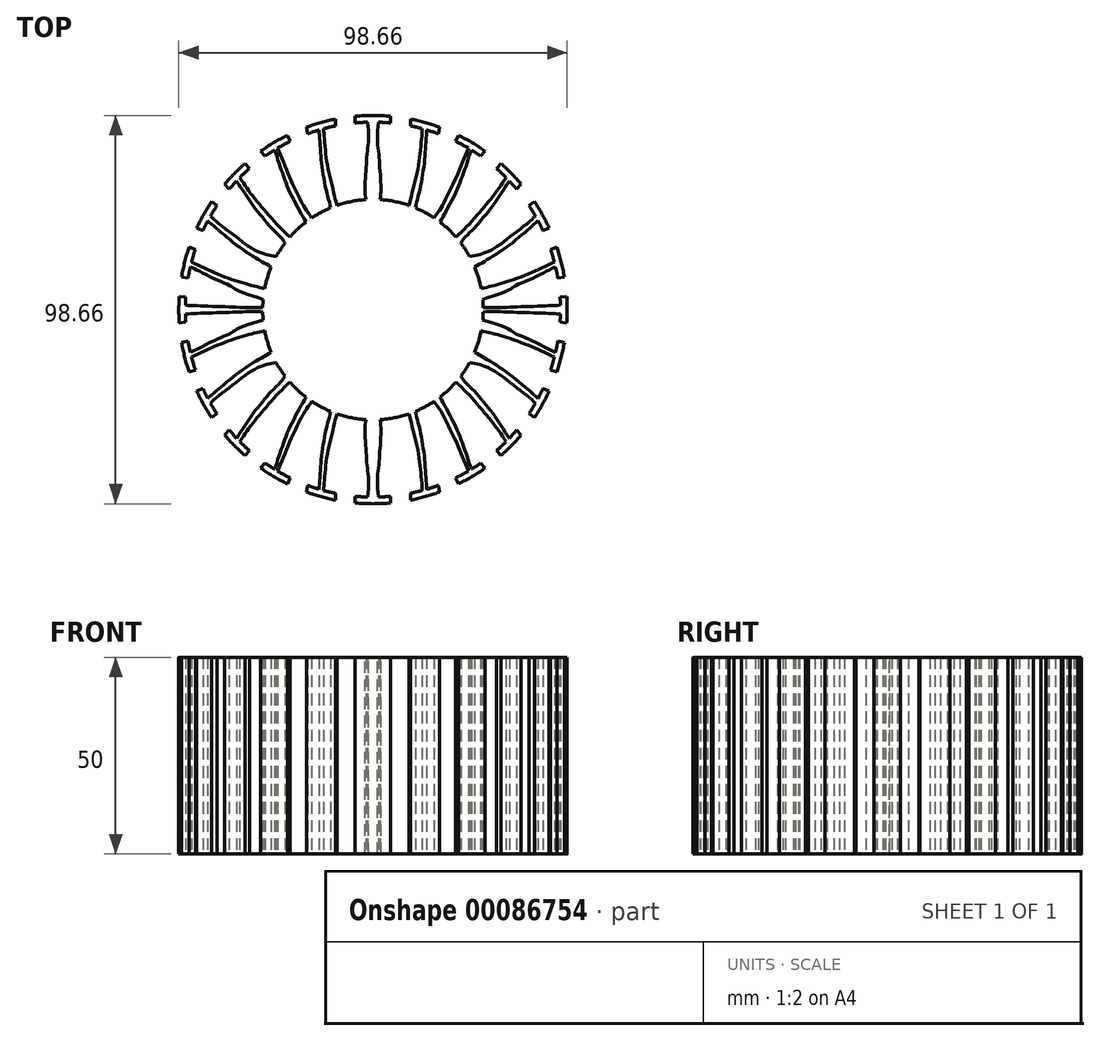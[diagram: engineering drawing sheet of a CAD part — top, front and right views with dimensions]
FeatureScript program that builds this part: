
annotation { "Feature Type Name" : "Feature", "Feature Type Description" : "" }
export const myFeature = defineFeature(function(context is Context, id is Id, definition is map)
    precondition{}
    {
        {
            var Q0;
            Q0=qCreatedBy(makeId("Top.planeOp"),FACE);
            var sketch = newSketch(context, id + "F0", { "sketchPlane" : qUnion([Q0])});
            skArc(sketch, "E0", {"start": v(49.33, 0) * mm, "mid": v(49.3, 1.68) * mm, "end": v(49.21, 3.35) * mm});
            skArc(sketch, "E1", {"start": v(47.63, 1.14) * mm, "mid": v(47.6, 2.16) * mm, "end": v(47.54, 3.17) * mm});
            skLineSegment(sketch, "E2", {"start": v(4.53, 49.12) * mm, "end": v(4.51, 47.43) * mm});
            skLineSegment(sketch, "E3", {"start": v(9.49, 48.4) * mm, "end": v(9.49, 46.69) * mm});
            skLineSegment(sketch, "E4", {"start": v(16.87, 46.35) * mm, "end": v(16.66, 44.64) * mm});
            skLineSegment(sketch, "E5", {"start": v(21.74, 44.28) * mm, "end": v(21, 42.77) * mm});
            skLineSegment(sketch, "E6", {"start": v(28.5, 40.26) * mm, "end": v(27.37, 39) * mm});
            skLineSegment(sketch, "E7", {"start": v(32.51, 37.1) * mm, "end": v(31.39, 35.84) * mm});
            skLineSegment(sketch, "E8", {"start": v(37.66, 31.86) * mm, "end": v(36.52, 30.6) * mm});
            skLineSegment(sketch, "E9", {"start": v(40.98, 27.45) * mm, "end": v(39.63, 26.45) * mm});
            skLineSegment(sketch, "E10", {"start": v(44.76, 20.73) * mm, "end": v(43.2, 20.07) * mm});
            skLineSegment(sketch, "E11", {"start": v(46.7, 15.88) * mm, "end": v(45.12, 15.3) * mm});
            skLineSegment(sketch, "E12", {"start": v(48.62, 8.32) * mm, "end": v(46.97, 8) * mm});
            skLineSegment(sketch, "E13", {"start": v(49.21, 3.35) * mm, "end": v(47.54, 3.17) * mm});
            skArc(sketch, "E14.trimOffspring", {"start": v(4.51, 47.43) * mm, "mid": v(2.94, 47.55) * mm, "end": v(1.37, 47.62) * mm});
            skArc(sketch, "E15.trimOffspring", {"start": v(4.53, 49.12) * mm, "mid": v(2.27, 49.28) * mm, "end": v(0, 49.33) * mm});
            skArc(sketch, "E16.trimOffspring", {"start": v(16.66, 44.64) * mm, "mid": v(15.17, 45.16) * mm, "end": v(13.66, 45.64) * mm});
            skArc(sketch, "E17.trimOffspring", {"start": v(16.87, 46.35) * mm, "mid": v(13.22, 47.52) * mm, "end": v(9.49, 48.4) * mm});
            skArc(sketch, "E18.trimOffspring", {"start": v(28.5, 40.26) * mm, "mid": v(25.2, 42.4) * mm, "end": v(21.74, 44.28) * mm});
            skArc(sketch, "E19.trimOffspring", {"start": v(27.37, 39) * mm, "mid": v(26.22, 39.78) * mm, "end": v(25.04, 40.53) * mm});
            skArc(sketch, "E20.trimOffspring", {"start": v(37.66, 31.86) * mm, "mid": v(35.18, 34.58) * mm, "end": v(32.51, 37.1) * mm});
            skArc(sketch, "E21.trimOffspring", {"start": v(36.52, 30.6) * mm, "mid": v(35.6, 31.66) * mm, "end": v(34.65, 32.7) * mm});
            skArc(sketch, "E22.trimOffspring", {"start": v(44.76, 20.73) * mm, "mid": v(43, 24.16) * mm, "end": v(40.98, 27.45) * mm});
            skArc(sketch, "E23.trimOffspring", {"start": v(43.2, 20.07) * mm, "mid": v(42.6, 21.32) * mm, "end": v(41.96, 22.56) * mm});
            skArc(sketch, "E24.trimOffspring", {"start": v(46.97, 8) * mm, "mid": v(46.7, 9.44) * mm, "end": v(46.39, 10.88) * mm});
            skArc(sketch, "E25.trimOffspring", {"start": v(48.62, 8.32) * mm, "mid": v(47.81, 12.13) * mm, "end": v(46.7, 15.88) * mm});
            skArc(sketch, "E26", {"start": v(9.1, 26.5) * mm, "mid": v(5.5, 27.47) * mm, "end": v(1.8, 27.96) * mm});
            skFitSpline(sketch, "E27", {"points": [v(1.8, 27.96) * mm, v(2, 30.15) * mm, v(1.92, 33.46) * mm, v(1.67, 37.11) * mm, v(1.46, 40.09) * mm, v(1.12, 42.89) * mm, v(1.37, 47.62) * mm], "startDerivative": vector(2.02, 15.22) * mm, "endDerivative": vector(2.38, 25.01) * mm});
            skFitSpline(sketch, "E28", {"points": [v(12.5, 45.97) * mm, v(12.42, 44.08) * mm, v(12.08, 40.51) * mm, v(11.48, 36.1) * mm, v(10.3, 31.08) * mm, v(9.49, 27.64) * mm, v(9.1, 26.5) * mm], "startDerivative": vector(-0.43, -13.47) * mm, "endDerivative": vector(-3.66, -9.72) * mm});
            skFitSpline(sketch, "E29", {"points": [v(10.76, 25.86) * mm, v(11.23, 27.85) * mm, v(11.95, 30.57) * mm, v(12.59, 34.05) * mm, v(13.1, 37.62) * mm, v(13.3, 40.85) * mm, v(13.56, 43.87) * mm, v(13.66, 45.64) * mm], "startDerivative": vector(3.52, 15.97) * mm, "endDerivative": vector(0.48, 14.42) * mm});
            skFitSpline(sketch, "E30", {"points": [v(24.26, 41) * mm, v(22.57, 36.98) * mm, v(20.7, 32.6) * mm, v(19.17, 29.47) * mm, v(17.56, 26.28) * mm, v(16.28, 24.41) * mm, v(15.54, 23.31) * mm], "startDerivative": vector(-8.46, -20.08) * mm, "endDerivative": vector(-6.5, -9.86) * mm});
            skFitSpline(sketch, "E31", {"points": [v(17, 22.26) * mm, v(18.28, 24.45) * mm, v(20.15, 27.98) * mm, v(21.76, 31.38) * mm, v(22.87, 34.35) * mm, v(23.89, 37.15) * mm, v(24.7, 39.79) * mm, v(25.04, 40.53) * mm], "startDerivative": vector(8.93, 14.97) * mm, "endDerivative": vector(4.14, 7.56) * mm});
            skFitSpline(sketch, "E32", {"points": [v(21.1, 18.43) * mm, v(24.01, 21.27) * mm, v(26.99, 24.58) * mm, v(29.37, 27.43) * mm, v(31.53, 30.15) * mm, v(33.02, 32.31) * mm, v(33.83, 33.55) * mm], "startDerivative": vector(15.59, 14.62) * mm, "endDerivative": vector(6.66, 10.2) * mm});
            skFitSpline(sketch, "E33", {"points": [v(34.65, 32.7) * mm, v(32.33, 29.17) * mm, v(30.23, 26.13) * mm, v(27.73, 23.02) * mm, v(25.4, 20.35) * mm, v(23.37, 18.37) * mm, v(22.34, 16.9) * mm], "startDerivative": vector(-12.39, -19.06) * mm, "endDerivative": vector(-7.33, -11.9) * mm});
            skFitSpline(sketch, "E34", {"points": [v(24.55, 13.49) * mm, v(26.54, 13.83) * mm, v(28.7, 14.51) * mm, v(32.04, 16.38) * mm, v(35.67, 19.22) * mm, v(39.64, 22.22) * mm, v(41.26, 23.83) * mm], "startDerivative": vector(15.26, 2.35) * mm, "endDerivative": vector(9.78, 10.81) * mm});
            skFitSpline(sketch, "E35", {"points": [v(41.96, 22.56) * mm, v(39.36, 20.3) * mm, v(34.3, 16.15) * mm, v(28.98, 12.64) * mm, v(25.83, 10.85) * mm], "startDerivative": vector(-11.26, -9.89) * mm, "endDerivative": vector(-13.8, -7.6) * mm});
            skFitSpline(sketch, "E36", {"points": [v(27.5, 5.38) * mm, v(31.98, 6.46) * mm, v(39.24, 8.95) * mm, v(46.08, 12.1) * mm], "startDerivative": vector(15.05, 3.25) * mm, "endDerivative": vector(18.54, 9.06) * mm});
            skFitSpline(sketch, "E37", {"points": [v(46.39, 10.88) * mm, v(44.54, 9.96) * mm, v(39.57, 7.5) * mm, v(36.08, 6) * mm, v(34.72, 5.06) * mm, v(27.9, 2.6) * mm], "startDerivative": vector(-10.67, -5.18) * mm, "endDerivative": vector(-30.07, -9.49) * mm});
            skFitSpline(sketch, "E38", {"points": [v(47.63, 1.14) * mm, v(43.46, 0.92) * mm, v(36.2, 0.67) * mm, v(31.63, 0.53) * mm, v(28, 0.56) * mm], "startDerivative": vector(-16.21, -0.96) * mm, "endDerivative": vector(-16.65, 0.32) * mm});
            skArc(sketch, "E39.trimOffspring", {"start": v(46.08, 12.1) * mm, "mid": v(45.63, 13.7) * mm, "end": v(45.12, 15.3) * mm});
            skArc(sketch, "E40.trimOffspring", {"start": v(41.26, 23.83) * mm, "mid": v(40.46, 25.15) * mm, "end": v(39.63, 26.45) * mm});
            skArc(sketch, "E41.trimOffspring", {"start": v(33.83, 33.55) * mm, "mid": v(32.63, 34.72) * mm, "end": v(31.39, 35.84) * mm});
            skArc(sketch, "E42.trimOffspring", {"start": v(24.26, 41) * mm, "mid": v(22.64, 41.92) * mm, "end": v(21, 42.77) * mm});
            skArc(sketch, "E43.trimOffspring", {"start": v(12.5, 45.97) * mm, "mid": v(11, 46.35) * mm, "end": v(9.49, 46.69) * mm});
            skArc(sketch, "E44.trimOffspring", {"start": v(15.54, 23.31) * mm, "mid": v(13.21, 24.7) * mm, "end": v(10.76, 25.86) * mm});
            skArc(sketch, "E45.trimOffspring", {"start": v(21.1, 18.43) * mm, "mid": v(19.15, 20.45) * mm, "end": v(17, 22.26) * mm});
            skArc(sketch, "E46.trimOffspring", {"start": v(24.55, 13.49) * mm, "mid": v(23.5, 15.23) * mm, "end": v(22.34, 16.9) * mm});
            skArc(sketch, "E47.trimOffspring", {"start": v(27.5, 5.38) * mm, "mid": v(26.8, 8.16) * mm, "end": v(25.83, 10.85) * mm});
            skArc(sketch, "E48.trimOffspring", {"start": v(28, 0.56) * mm, "mid": v(27.97, 1.58) * mm, "end": v(27.9, 2.6) * mm});
            skLineSegment(sketch, "E49", {"start": v(0, 49.33) * mm, "end": v(0, 0) * mm});
            skLineSegment(sketch, "E50", {"start": v(49.33, 0) * mm, "end": v(0, 0) * mm});
            skArc(sketch, "E51.MirrorCS", {"start": v(-28, 0.56) * mm, "mid": v(-27.97, 1.58) * mm, "end": v(-27.9, 2.6) * mm});
            skArc(sketch, "E52.MirrorCS", {"start": v(-27.37, 39) * mm, "mid": v(-26.22, 39.78) * mm, "end": v(-25.04, 40.53) * mm});
            skArc(sketch, "E53.MirrorCS", {"start": v(-12.5, 45.97) * mm, "mid": v(-11, 46.35) * mm, "end": v(-9.49, 46.69) * mm});
            skArc(sketch, "E54.MirrorCS", {"start": v(-16.66, 44.64) * mm, "mid": v(-15.17, 45.16) * mm, "end": v(-13.66, 45.64) * mm});
            skArc(sketch, "E55.MirrorCS", {"start": v(-41.26, 23.83) * mm, "mid": v(-40.46, 25.15) * mm, "end": v(-39.63, 26.45) * mm});
            skArc(sketch, "E56.MirrorCS", {"start": v(-16.87, 46.35) * mm, "mid": v(-13.22, 47.52) * mm, "end": v(-9.49, 48.4) * mm});
            skArc(sketch, "E57.MirrorCS", {"start": v(-21.1, 18.43) * mm, "mid": v(-19.15, 20.45) * mm, "end": v(-17, 22.26) * mm});
            skArc(sketch, "E58.MirrorCS", {"start": v(-15.54, 23.31) * mm, "mid": v(-13.21, 24.7) * mm, "end": v(-10.76, 25.86) * mm});
            skArc(sketch, "E59.MirrorCS", {"start": v(-36.52, 30.6) * mm, "mid": v(-35.6, 31.66) * mm, "end": v(-34.65, 32.7) * mm});
            skArc(sketch, "E60.MirrorCS", {"start": v(-24.55, 13.49) * mm, "mid": v(-23.5, 15.23) * mm, "end": v(-22.34, 16.9) * mm});
            skArc(sketch, "E61.MirrorCS", {"start": v(-27.5, 5.38) * mm, "mid": v(-26.8, 8.16) * mm, "end": v(-25.83, 10.85) * mm});
            skLineSegment(sketch, "E62.MirrorCS", {"start": v(-49.21, 3.35) * mm, "end": v(-47.54, 3.17) * mm});
            skArc(sketch, "E63.MirrorCS", {"start": v(-4.51, 47.43) * mm, "mid": v(-2.94, 47.55) * mm, "end": v(-1.37, 47.62) * mm});
            skArc(sketch, "E64.MirrorCS", {"start": v(-4.53, 49.12) * mm, "mid": v(-2.27, 49.28) * mm, "end": v(0, 49.33) * mm});
            skArc(sketch, "E65.MirrorCS", {"start": v(-49.33, 0) * mm, "mid": v(-49.3, 1.68) * mm, "end": v(-49.21, 3.35) * mm});
            skArc(sketch, "E66.MirrorCS", {"start": v(-47.63, 1.14) * mm, "mid": v(-47.6, 2.16) * mm, "end": v(-47.54, 3.17) * mm});
            skLineSegment(sketch, "E67.MirrorCS", {"start": v(-16.87, 46.35) * mm, "end": v(-16.66, 44.64) * mm});
            skLineSegment(sketch, "E68.MirrorCS", {"start": v(-44.76, 20.73) * mm, "end": v(-43.2, 20.07) * mm});
            skArc(sketch, "E69.MirrorCS", {"start": v(-43.2, 20.07) * mm, "mid": v(-42.6, 21.32) * mm, "end": v(-41.96, 22.56) * mm});
            skArc(sketch, "E70.MirrorCS", {"start": v(-33.83, 33.55) * mm, "mid": v(-32.63, 34.72) * mm, "end": v(-31.39, 35.84) * mm});
            skArc(sketch, "E71.MirrorCS", {"start": v(-24.26, 41) * mm, "mid": v(-22.64, 41.92) * mm, "end": v(-21, 42.77) * mm});
            skArc(sketch, "E72.MirrorCS", {"start": v(-37.66, 31.86) * mm, "mid": v(-35.18, 34.58) * mm, "end": v(-32.51, 37.1) * mm});
            skArc(sketch, "E73.MirrorCS", {"start": v(-44.76, 20.73) * mm, "mid": v(-43, 24.16) * mm, "end": v(-40.98, 27.45) * mm});
            skLineSegment(sketch, "E74.MirrorCS", {"start": v(-4.53, 49.12) * mm, "end": v(-4.51, 47.43) * mm});
            skLineSegment(sketch, "E75.MirrorCS", {"start": v(-9.49, 48.4) * mm, "end": v(-9.49, 46.69) * mm});
            skLineSegment(sketch, "E76.MirrorCS", {"start": v(-21.74, 44.28) * mm, "end": v(-21, 42.77) * mm});
            skLineSegment(sketch, "E77.MirrorCS", {"start": v(-28.5, 40.26) * mm, "end": v(-27.37, 39) * mm});
            skLineSegment(sketch, "E78.MirrorCS", {"start": v(-32.51, 37.1) * mm, "end": v(-31.39, 35.84) * mm});
            skLineSegment(sketch, "E79.MirrorCS", {"start": v(-37.66, 31.86) * mm, "end": v(-36.52, 30.6) * mm});
            skLineSegment(sketch, "E80.MirrorCS", {"start": v(-40.98, 27.45) * mm, "end": v(-39.63, 26.45) * mm});
            skLineSegment(sketch, "E81.MirrorCS", {"start": v(-46.7, 15.88) * mm, "end": v(-45.12, 15.3) * mm});
            skLineSegment(sketch, "E82.MirrorCS", {"start": v(-48.62, 8.32) * mm, "end": v(-46.97, 8) * mm});
            skArc(sketch, "E83.MirrorCS", {"start": v(-46.08, 12.1) * mm, "mid": v(-45.63, 13.7) * mm, "end": v(-45.12, 15.3) * mm});
            skArc(sketch, "E84.MirrorCS", {"start": v(-46.97, 8) * mm, "mid": v(-46.7, 9.44) * mm, "end": v(-46.39, 10.88) * mm});
            skArc(sketch, "E85.MirrorCS", {"start": v(-48.62, 8.32) * mm, "mid": v(-47.81, 12.13) * mm, "end": v(-46.7, 15.88) * mm});
            skArc(sketch, "E86.MirrorCS", {"start": v(-28.5, 40.26) * mm, "mid": v(-25.2, 42.4) * mm, "end": v(-21.74, 44.28) * mm});
            skArc(sketch, "E87.MirrorCS", {"start": v(-9.1, 26.5) * mm, "mid": v(-5.5, 27.47) * mm, "end": v(-1.8, 27.96) * mm});
            skFitSpline(sketch, "E88.MirrorCS", {"points": [v(-41.96, 22.56) * mm, v(-39.36, 20.3) * mm, v(-34.3, 16.15) * mm, v(-28.98, 12.64) * mm, v(-25.83, 10.85) * mm], "startDerivative": vector(11.26, -9.89) * mm, "endDerivative": vector(13.8, -7.6) * mm});
            skFitSpline(sketch, "E89.MirrorCS", {"points": [v(-1.8, 27.96) * mm, v(-2, 30.15) * mm, v(-1.92, 33.46) * mm, v(-1.67, 37.11) * mm, v(-1.46, 40.09) * mm, v(-1.12, 42.89) * mm, v(-1.37, 47.62) * mm], "startDerivative": vector(-2.02, 15.22) * mm, "endDerivative": vector(-2.38, 25.01) * mm});
            skFitSpline(sketch, "E90.MirrorCS", {"points": [v(-10.76, 25.86) * mm, v(-11.23, 27.85) * mm, v(-11.95, 30.57) * mm, v(-12.59, 34.05) * mm, v(-13.1, 37.62) * mm, v(-13.3, 40.85) * mm, v(-13.56, 43.87) * mm, v(-13.66, 45.64) * mm], "startDerivative": vector(-3.52, 15.97) * mm, "endDerivative": vector(-0.48, 14.42) * mm});
            skFitSpline(sketch, "E91.MirrorCS", {"points": [v(-27.5, 5.38) * mm, v(-31.98, 6.46) * mm, v(-39.24, 8.95) * mm, v(-46.08, 12.1) * mm], "startDerivative": vector(-15.05, 3.25) * mm, "endDerivative": vector(-18.54, 9.06) * mm});
            skFitSpline(sketch, "E92.MirrorCS", {"points": [v(-12.5, 45.97) * mm, v(-12.42, 44.08) * mm, v(-12.08, 40.51) * mm, v(-11.48, 36.1) * mm, v(-10.3, 31.08) * mm, v(-9.49, 27.64) * mm, v(-9.1, 26.5) * mm], "startDerivative": vector(0.43, -13.47) * mm, "endDerivative": vector(3.66, -9.72) * mm});
            skFitSpline(sketch, "E93.MirrorCS", {"points": [v(-24.26, 41) * mm, v(-22.57, 36.98) * mm, v(-20.7, 32.6) * mm, v(-19.17, 29.47) * mm, v(-17.56, 26.28) * mm, v(-16.28, 24.41) * mm, v(-15.54, 23.31) * mm], "startDerivative": vector(8.46, -20.08) * mm, "endDerivative": vector(6.5, -9.86) * mm});
            skFitSpline(sketch, "E94.MirrorCS", {"points": [v(-46.39, 10.88) * mm, v(-44.54, 9.96) * mm, v(-39.57, 7.5) * mm, v(-36.08, 6) * mm, v(-34.72, 5.06) * mm, v(-27.9, 2.6) * mm], "startDerivative": vector(10.67, -5.18) * mm, "endDerivative": vector(30.07, -9.49) * mm});
            skFitSpline(sketch, "E95.MirrorCS", {"points": [v(-17, 22.26) * mm, v(-18.28, 24.45) * mm, v(-20.15, 27.98) * mm, v(-21.76, 31.38) * mm, v(-22.87, 34.35) * mm, v(-23.89, 37.15) * mm, v(-24.7, 39.79) * mm, v(-25.04, 40.53) * mm], "startDerivative": vector(-8.93, 14.97) * mm, "endDerivative": vector(-4.14, 7.56) * mm});
            skFitSpline(sketch, "E96.MirrorCS", {"points": [v(-21.1, 18.43) * mm, v(-24.01, 21.27) * mm, v(-26.99, 24.58) * mm, v(-29.37, 27.43) * mm, v(-31.53, 30.15) * mm, v(-33.02, 32.31) * mm, v(-33.83, 33.55) * mm], "startDerivative": vector(-15.59, 14.62) * mm, "endDerivative": vector(-6.66, 10.2) * mm});
            skFitSpline(sketch, "E97.MirrorCS", {"points": [v(-34.65, 32.7) * mm, v(-32.33, 29.17) * mm, v(-30.23, 26.13) * mm, v(-27.73, 23.02) * mm, v(-25.4, 20.35) * mm, v(-23.37, 18.37) * mm, v(-22.34, 16.9) * mm], "startDerivative": vector(12.39, -19.06) * mm, "endDerivative": vector(7.33, -11.9) * mm});
            skFitSpline(sketch, "E98.MirrorCS", {"points": [v(-24.55, 13.49) * mm, v(-26.54, 13.83) * mm, v(-28.7, 14.51) * mm, v(-32.04, 16.38) * mm, v(-35.67, 19.22) * mm, v(-39.64, 22.22) * mm, v(-41.26, 23.83) * mm], "startDerivative": vector(-15.26, 2.35) * mm, "endDerivative": vector(-9.78, 10.81) * mm});
            skFitSpline(sketch, "E99.MirrorCS", {"points": [v(-47.63, 1.14) * mm, v(-43.46, 0.92) * mm, v(-36.2, 0.67) * mm, v(-31.63, 0.53) * mm, v(-28, 0.56) * mm], "startDerivative": vector(16.21, -0.96) * mm, "endDerivative": vector(16.65, 0.32) * mm});
            skLineSegment(sketch, "E100.MirrorCS", {"start": v(-49.33, 0) * mm, "end": v(0, 0) * mm});
            skLineSegment(sketch, "E101", {"start": v(0, 0) * mm, "end": v(-91, 0) * mm, "construction": true});
            skArc(sketch, "E102.MirrorCS", {"start": v(-47.63, -1.14) * mm, "mid": v(-47.6, -2.16) * mm, "end": v(-47.54, -3.17) * mm});
            skArc(sketch, "E103.MirrorCS", {"start": v(-33.83, -33.55) * mm, "mid": v(-32.63, -34.72) * mm, "end": v(-31.39, -35.84) * mm});
            skLineSegment(sketch, "E104.MirrorCS", {"start": v(-44.76, -20.73) * mm, "end": v(-43.2, -20.07) * mm});
            skArc(sketch, "E105.MirrorCS", {"start": v(-28, -0.56) * mm, "mid": v(-27.97, -1.58) * mm, "end": v(-27.9, -2.6) * mm});
            skArc(sketch, "E106.MirrorCS", {"start": v(27.37, -39) * mm, "mid": v(26.22, -39.78) * mm, "end": v(25.04, -40.53) * mm});
            skArc(sketch, "E107.MirrorCS", {"start": v(-36.52, -30.6) * mm, "mid": v(-35.6, -31.66) * mm, "end": v(-34.65, -32.7) * mm});
            skLineSegment(sketch, "E108.MirrorCS", {"start": v(-49.21, -3.35) * mm, "end": v(-47.54, -3.17) * mm});
            skLineSegment(sketch, "E109.MirrorCS", {"start": v(-37.66, -31.86) * mm, "end": v(-36.52, -30.6) * mm});
            skLineSegment(sketch, "E110.MirrorCS", {"start": v(49.21, -3.35) * mm, "end": v(47.54, -3.17) * mm});
            skArc(sketch, "E111.MirrorCS", {"start": v(49.33, 0) * mm, "mid": v(49.3, -1.68) * mm, "end": v(49.21, -3.35) * mm});
            skArc(sketch, "E112.MirrorCS", {"start": v(47.63, -1.14) * mm, "mid": v(47.6, -2.16) * mm, "end": v(47.54, -3.17) * mm});
            skArc(sketch, "E113.MirrorCS", {"start": v(28, -0.56) * mm, "mid": v(27.97, -1.58) * mm, "end": v(27.9, -2.6) * mm});
            skArc(sketch, "E114.MirrorCS", {"start": v(-49.33, 0) * mm, "mid": v(-49.3, -1.68) * mm, "end": v(-49.21, -3.35) * mm});
            skArc(sketch, "E115.MirrorCS", {"start": v(-24.26, -41) * mm, "mid": v(-22.64, -41.92) * mm, "end": v(-21, -42.77) * mm});
            skArc(sketch, "E116.MirrorCS", {"start": v(43.2, -20.07) * mm, "mid": v(42.6, -21.32) * mm, "end": v(41.96, -22.56) * mm});
            skArc(sketch, "E117.MirrorCS", {"start": v(46.08, -12.1) * mm, "mid": v(45.63, -13.7) * mm, "end": v(45.12, -15.3) * mm});
            skArc(sketch, "E118.MirrorCS", {"start": v(-41.26, -23.83) * mm, "mid": v(-40.46, -25.15) * mm, "end": v(-39.63, -26.45) * mm});
            skArc(sketch, "E119.MirrorCS", {"start": v(-16.66, -44.64) * mm, "mid": v(-15.17, -45.16) * mm, "end": v(-13.66, -45.64) * mm});
            skArc(sketch, "E120.MirrorCS", {"start": v(24.26, -41) * mm, "mid": v(22.64, -41.92) * mm, "end": v(21, -42.77) * mm});
            skArc(sketch, "E121.MirrorCS", {"start": v(44.76, -20.73) * mm, "mid": v(43, -24.16) * mm, "end": v(40.98, -27.45) * mm});
            skArc(sketch, "E122.MirrorCS", {"start": v(-15.54, -23.31) * mm, "mid": v(-13.21, -24.7) * mm, "end": v(-10.76, -25.86) * mm});
            skArc(sketch, "E123.MirrorCS", {"start": v(-12.5, -45.97) * mm, "mid": v(-11, -46.35) * mm, "end": v(-9.49, -46.69) * mm});
            skArc(sketch, "E124.MirrorCS", {"start": v(-43.2, -20.07) * mm, "mid": v(-42.6, -21.32) * mm, "end": v(-41.96, -22.56) * mm});
            skArc(sketch, "E125.MirrorCS", {"start": v(36.52, -30.6) * mm, "mid": v(35.6, -31.66) * mm, "end": v(34.65, -32.7) * mm});
            skArc(sketch, "E126.MirrorCS", {"start": v(-44.76, -20.73) * mm, "mid": v(-43, -24.16) * mm, "end": v(-40.98, -27.45) * mm});
            skArc(sketch, "E127.MirrorCS", {"start": v(33.83, -33.55) * mm, "mid": v(32.63, -34.72) * mm, "end": v(31.39, -35.84) * mm});
            skArc(sketch, "E128.MirrorCS", {"start": v(-21.1, -18.43) * mm, "mid": v(-19.15, -20.45) * mm, "end": v(-17, -22.26) * mm});
            skArc(sketch, "E129.MirrorCS", {"start": v(-27.37, -39) * mm, "mid": v(-26.22, -39.78) * mm, "end": v(-25.04, -40.53) * mm});
            skArc(sketch, "E130.MirrorCS", {"start": v(-46.97, -8) * mm, "mid": v(-46.7, -9.44) * mm, "end": v(-46.39, -10.88) * mm});
            skLineSegment(sketch, "E131.MirrorCS", {"start": v(-16.87, -46.35) * mm, "end": v(-16.66, -44.64) * mm});
            skArc(sketch, "E132.MirrorCS", {"start": v(-46.08, -12.1) * mm, "mid": v(-45.63, -13.7) * mm, "end": v(-45.12, -15.3) * mm});
            skArc(sketch, "E133.MirrorCS", {"start": v(46.97, -8) * mm, "mid": v(46.7, -9.44) * mm, "end": v(46.39, -10.88) * mm});
            skArc(sketch, "E134.MirrorCS", {"start": v(41.26, -23.83) * mm, "mid": v(40.46, -25.15) * mm, "end": v(39.63, -26.45) * mm});
            skArc(sketch, "E135.MirrorCS", {"start": v(-16.87, -46.35) * mm, "mid": v(-13.22, -47.52) * mm, "end": v(-9.49, -48.4) * mm});
            skArc(sketch, "E136.MirrorCS", {"start": v(12.5, -45.97) * mm, "mid": v(11, -46.35) * mm, "end": v(9.49, -46.69) * mm});
            skArc(sketch, "E137.MirrorCS", {"start": v(-27.5, -5.38) * mm, "mid": v(-26.8, -8.16) * mm, "end": v(-25.83, -10.85) * mm});
            skArc(sketch, "E138.MirrorCS", {"start": v(21.1, -18.43) * mm, "mid": v(19.15, -20.45) * mm, "end": v(17, -22.26) * mm});
            skArc(sketch, "E139.MirrorCS", {"start": v(-24.55, -13.49) * mm, "mid": v(-23.5, -15.23) * mm, "end": v(-22.34, -16.9) * mm});
            skArc(sketch, "E140.MirrorCS", {"start": v(15.54, -23.31) * mm, "mid": v(13.21, -24.7) * mm, "end": v(10.76, -25.86) * mm});
            skArc(sketch, "E141.MirrorCS", {"start": v(24.55, -13.49) * mm, "mid": v(23.5, -15.23) * mm, "end": v(22.34, -16.9) * mm});
            skArc(sketch, "E142.MirrorCS", {"start": v(27.5, -5.38) * mm, "mid": v(26.8, -8.16) * mm, "end": v(25.83, -10.85) * mm});
            skLineSegment(sketch, "E143.MirrorCS", {"start": v(37.66, -31.86) * mm, "end": v(36.52, -30.6) * mm});
            skLineSegment(sketch, "E144.MirrorCS", {"start": v(44.76, -20.73) * mm, "end": v(43.2, -20.07) * mm});
            skArc(sketch, "E145.MirrorCS", {"start": v(4.53, -49.12) * mm, "mid": v(2.27, -49.28) * mm, "end": v(0, -49.33) * mm});
            skLineSegment(sketch, "E146.MirrorCS", {"start": v(28.5, -40.26) * mm, "end": v(27.37, -39) * mm});
            skLineSegment(sketch, "E147.MirrorCS", {"start": v(-48.62, -8.32) * mm, "end": v(-46.97, -8) * mm});
            skLineSegment(sketch, "E148.MirrorCS", {"start": v(-4.53, -49.12) * mm, "end": v(-4.51, -47.43) * mm});
            skArc(sketch, "E149.MirrorCS", {"start": v(-28.5, -40.26) * mm, "mid": v(-25.2, -42.4) * mm, "end": v(-21.74, -44.28) * mm});
            skArc(sketch, "E150.MirrorCS", {"start": v(-48.62, -8.32) * mm, "mid": v(-47.81, -12.13) * mm, "end": v(-46.7, -15.88) * mm});
            skArc(sketch, "E151.MirrorCS", {"start": v(48.62, -8.32) * mm, "mid": v(47.81, -12.13) * mm, "end": v(46.7, -15.88) * mm});
            skArc(sketch, "E152.MirrorCS", {"start": v(37.66, -31.86) * mm, "mid": v(35.18, -34.58) * mm, "end": v(32.51, -37.1) * mm});
            skArc(sketch, "E153.MirrorCS", {"start": v(-37.66, -31.86) * mm, "mid": v(-35.18, -34.58) * mm, "end": v(-32.51, -37.1) * mm});
            skLineSegment(sketch, "E154.MirrorCS", {"start": v(-28.5, -40.26) * mm, "end": v(-27.37, -39) * mm});
            skLineSegment(sketch, "E155.MirrorCS", {"start": v(-21.74, -44.28) * mm, "end": v(-21, -42.77) * mm});
            skLineSegment(sketch, "E156.MirrorCS", {"start": v(-32.51, -37.1) * mm, "end": v(-31.39, -35.84) * mm});
            skArc(sketch, "E157.MirrorCS", {"start": v(-4.51, -47.43) * mm, "mid": v(-2.94, -47.55) * mm, "end": v(-1.37, -47.62) * mm});
            skLineSegment(sketch, "E158.MirrorCS", {"start": v(32.51, -37.1) * mm, "end": v(31.39, -35.84) * mm});
            skArc(sketch, "E159.MirrorCS", {"start": v(4.51, -47.43) * mm, "mid": v(2.94, -47.55) * mm, "end": v(1.37, -47.62) * mm});
            skLineSegment(sketch, "E160.MirrorCS", {"start": v(4.53, -49.12) * mm, "end": v(4.51, -47.43) * mm});
            skLineSegment(sketch, "E161.MirrorCS", {"start": v(9.49, -48.4) * mm, "end": v(9.49, -46.69) * mm});
            skLineSegment(sketch, "E162.MirrorCS", {"start": v(21.74, -44.28) * mm, "end": v(21, -42.77) * mm});
            skLineSegment(sketch, "E163.MirrorCS", {"start": v(16.87, -46.35) * mm, "end": v(16.66, -44.64) * mm});
            skLineSegment(sketch, "E164.MirrorCS", {"start": v(40.98, -27.45) * mm, "end": v(39.63, -26.45) * mm});
            skLineSegment(sketch, "E165.MirrorCS", {"start": v(46.7, -15.88) * mm, "end": v(45.12, -15.3) * mm});
            skLineSegment(sketch, "E166.MirrorCS", {"start": v(48.62, -8.32) * mm, "end": v(46.97, -8) * mm});
            skArc(sketch, "E167.MirrorCS", {"start": v(16.87, -46.35) * mm, "mid": v(13.22, -47.52) * mm, "end": v(9.49, -48.4) * mm});
            skLineSegment(sketch, "E168.MirrorCS", {"start": v(-46.7, -15.88) * mm, "end": v(-45.12, -15.3) * mm});
            skArc(sketch, "E169.MirrorCS", {"start": v(16.66, -44.64) * mm, "mid": v(15.17, -45.16) * mm, "end": v(13.66, -45.64) * mm});
            skLineSegment(sketch, "E170.MirrorCS", {"start": v(-40.98, -27.45) * mm, "end": v(-39.63, -26.45) * mm});
            skArc(sketch, "E171.MirrorCS", {"start": v(-4.53, -49.12) * mm, "mid": v(-2.27, -49.28) * mm, "end": v(0, -49.33) * mm});
            skArc(sketch, "E172.MirrorCS", {"start": v(28.5, -40.26) * mm, "mid": v(25.2, -42.4) * mm, "end": v(21.74, -44.28) * mm});
            skLineSegment(sketch, "E173.MirrorCS", {"start": v(-9.49, -48.4) * mm, "end": v(-9.49, -46.69) * mm});
            skArc(sketch, "E174.MirrorCS", {"start": v(-9.1, -26.5) * mm, "mid": v(-5.5, -27.47) * mm, "end": v(-1.8, -27.96) * mm});
            skFitSpline(sketch, "E175.MirrorCS", {"points": [v(-10.76, -25.86) * mm, v(-11.23, -27.85) * mm, v(-11.95, -30.57) * mm, v(-12.59, -34.05) * mm, v(-13.1, -37.62) * mm, v(-13.3, -40.85) * mm, v(-13.56, -43.87) * mm, v(-13.66, -45.64) * mm], "startDerivative": vector(-3.52, -15.97) * mm, "endDerivative": vector(-0.48, -14.42) * mm});
            skArc(sketch, "E176.MirrorCS", {"start": v(9.1, -26.5) * mm, "mid": v(5.5, -27.47) * mm, "end": v(1.8, -27.96) * mm});
            skFitSpline(sketch, "E177.MirrorCS", {"points": [v(46.39, -10.88) * mm, v(44.54, -9.96) * mm, v(39.57, -7.5) * mm, v(36.08, -6) * mm, v(34.72, -5.06) * mm, v(27.9, -2.6) * mm], "startDerivative": vector(-10.67, 5.18) * mm, "endDerivative": vector(-30.07, 9.49) * mm});
            skFitSpline(sketch, "E178.MirrorCS", {"points": [v(-1.8, -27.96) * mm, v(-2, -30.15) * mm, v(-1.92, -33.46) * mm, v(-1.67, -37.11) * mm, v(-1.46, -40.09) * mm, v(-1.12, -42.89) * mm, v(-1.37, -47.62) * mm], "startDerivative": vector(-2.02, -15.22) * mm, "endDerivative": vector(-2.38, -25.01) * mm});
            skFitSpline(sketch, "E179.MirrorCS", {"points": [v(27.5, -5.38) * mm, v(31.98, -6.46) * mm, v(39.24, -8.95) * mm, v(46.08, -12.1) * mm], "startDerivative": vector(15.05, -3.25) * mm, "endDerivative": vector(18.54, -9.06) * mm});
            skLineSegment(sketch, "E180.MirrorCS", {"start": v(0, -49.33) * mm, "end": v(0, 0) * mm});
            skFitSpline(sketch, "E181.MirrorCS", {"points": [v(41.96, -22.56) * mm, v(39.36, -20.3) * mm, v(34.3, -16.15) * mm, v(28.98, -12.64) * mm, v(25.83, -10.85) * mm], "startDerivative": vector(-11.26, 9.89) * mm, "endDerivative": vector(-13.8, 7.6) * mm});
            skFitSpline(sketch, "E182.MirrorCS", {"points": [v(-41.96, -22.56) * mm, v(-39.36, -20.3) * mm, v(-34.3, -16.15) * mm, v(-28.98, -12.64) * mm, v(-25.83, -10.85) * mm], "startDerivative": vector(11.26, 9.89) * mm, "endDerivative": vector(13.8, 7.6) * mm});
            skFitSpline(sketch, "E183.MirrorCS", {"points": [v(24.55, -13.49) * mm, v(26.54, -13.83) * mm, v(28.7, -14.51) * mm, v(32.04, -16.38) * mm, v(35.67, -19.22) * mm, v(39.64, -22.22) * mm, v(41.26, -23.83) * mm], "startDerivative": vector(15.26, -2.35) * mm, "endDerivative": vector(9.78, -10.81) * mm});
            skFitSpline(sketch, "E184.MirrorCS", {"points": [v(-24.55, -13.49) * mm, v(-26.54, -13.83) * mm, v(-28.7, -14.51) * mm, v(-32.04, -16.38) * mm, v(-35.67, -19.22) * mm, v(-39.64, -22.22) * mm, v(-41.26, -23.83) * mm], "startDerivative": vector(-15.26, -2.35) * mm, "endDerivative": vector(-9.78, -10.81) * mm});
            skFitSpline(sketch, "E185.MirrorCS", {"points": [v(1.8, -27.96) * mm, v(2, -30.15) * mm, v(1.92, -33.46) * mm, v(1.67, -37.11) * mm, v(1.46, -40.09) * mm, v(1.12, -42.89) * mm, v(1.37, -47.62) * mm], "startDerivative": vector(2.02, -15.22) * mm, "endDerivative": vector(2.38, -25.01) * mm});
            skFitSpline(sketch, "E186.MirrorCS", {"points": [v(-27.5, -5.38) * mm, v(-31.98, -6.46) * mm, v(-39.24, -8.95) * mm, v(-46.08, -12.1) * mm], "startDerivative": vector(-15.05, -3.25) * mm, "endDerivative": vector(-18.54, -9.06) * mm});
            skFitSpline(sketch, "E187.MirrorCS", {"points": [v(10.76, -25.86) * mm, v(11.23, -27.85) * mm, v(11.95, -30.57) * mm, v(12.59, -34.05) * mm, v(13.1, -37.62) * mm, v(13.3, -40.85) * mm, v(13.56, -43.87) * mm, v(13.66, -45.64) * mm], "startDerivative": vector(3.52, -15.97) * mm, "endDerivative": vector(0.48, -14.42) * mm});
            skFitSpline(sketch, "E188.MirrorCS", {"points": [v(-24.26, -41) * mm, v(-22.57, -36.98) * mm, v(-20.7, -32.6) * mm, v(-19.17, -29.47) * mm, v(-17.56, -26.28) * mm, v(-16.28, -24.41) * mm, v(-15.54, -23.31) * mm], "startDerivative": vector(8.46, 20.08) * mm, "endDerivative": vector(6.5, 9.86) * mm});
            skFitSpline(sketch, "E189.MirrorCS", {"points": [v(12.5, -45.97) * mm, v(12.42, -44.08) * mm, v(12.08, -40.51) * mm, v(11.48, -36.1) * mm, v(10.3, -31.08) * mm, v(9.49, -27.64) * mm, v(9.1, -26.5) * mm], "startDerivative": vector(-0.43, 13.47) * mm, "endDerivative": vector(-3.66, 9.72) * mm});
            skFitSpline(sketch, "E190.MirrorCS", {"points": [v(-12.5, -45.97) * mm, v(-12.42, -44.08) * mm, v(-12.08, -40.51) * mm, v(-11.48, -36.1) * mm, v(-10.3, -31.08) * mm, v(-9.49, -27.64) * mm, v(-9.1, -26.5) * mm], "startDerivative": vector(0.43, 13.47) * mm, "endDerivative": vector(3.66, 9.72) * mm});
            skFitSpline(sketch, "E191.MirrorCS", {"points": [v(24.26, -41) * mm, v(22.57, -36.98) * mm, v(20.7, -32.6) * mm, v(19.17, -29.47) * mm, v(17.56, -26.28) * mm, v(16.28, -24.41) * mm, v(15.54, -23.31) * mm], "startDerivative": vector(-8.46, 20.08) * mm, "endDerivative": vector(-6.5, 9.86) * mm});
            skFitSpline(sketch, "E192.MirrorCS", {"points": [v(-46.39, -10.88) * mm, v(-44.54, -9.96) * mm, v(-39.57, -7.5) * mm, v(-36.08, -6) * mm, v(-34.72, -5.06) * mm, v(-27.9, -2.6) * mm], "startDerivative": vector(10.67, 5.18) * mm, "endDerivative": vector(30.07, 9.49) * mm});
            skFitSpline(sketch, "E193.MirrorCS", {"points": [v(-17, -22.26) * mm, v(-18.28, -24.45) * mm, v(-20.15, -27.98) * mm, v(-21.76, -31.38) * mm, v(-22.87, -34.35) * mm, v(-23.89, -37.15) * mm, v(-24.7, -39.79) * mm, v(-25.04, -40.53) * mm], "startDerivative": vector(-8.93, -14.97) * mm, "endDerivative": vector(-4.14, -7.56) * mm});
            skFitSpline(sketch, "E194.MirrorCS", {"points": [v(17, -22.26) * mm, v(18.28, -24.45) * mm, v(20.15, -27.98) * mm, v(21.76, -31.38) * mm, v(22.87, -34.35) * mm, v(23.89, -37.15) * mm, v(24.7, -39.79) * mm, v(25.04, -40.53) * mm], "startDerivative": vector(8.93, -14.97) * mm, "endDerivative": vector(4.14, -7.56) * mm});
            skFitSpline(sketch, "E195.MirrorCS", {"points": [v(-21.1, -18.43) * mm, v(-24.01, -21.27) * mm, v(-26.99, -24.58) * mm, v(-29.37, -27.43) * mm, v(-31.53, -30.15) * mm, v(-33.02, -32.31) * mm, v(-33.83, -33.55) * mm], "startDerivative": vector(-15.59, -14.62) * mm, "endDerivative": vector(-6.66, -10.2) * mm});
            skFitSpline(sketch, "E196.MirrorCS", {"points": [v(21.1, -18.43) * mm, v(24.01, -21.27) * mm, v(26.99, -24.58) * mm, v(29.37, -27.43) * mm, v(31.53, -30.15) * mm, v(33.02, -32.31) * mm, v(33.83, -33.55) * mm], "startDerivative": vector(15.59, -14.62) * mm, "endDerivative": vector(6.66, -10.2) * mm});
            skFitSpline(sketch, "E197.MirrorCS", {"points": [v(34.65, -32.7) * mm, v(32.33, -29.17) * mm, v(30.23, -26.13) * mm, v(27.73, -23.02) * mm, v(25.4, -20.35) * mm, v(23.37, -18.37) * mm, v(22.34, -16.9) * mm], "startDerivative": vector(-12.39, 19.06) * mm, "endDerivative": vector(-7.33, 11.9) * mm});
            skFitSpline(sketch, "E198.MirrorCS", {"points": [v(-34.65, -32.7) * mm, v(-32.33, -29.17) * mm, v(-30.23, -26.13) * mm, v(-27.73, -23.02) * mm, v(-25.4, -20.35) * mm, v(-23.37, -18.37) * mm, v(-22.34, -16.9) * mm], "startDerivative": vector(12.39, 19.06) * mm, "endDerivative": vector(7.33, 11.9) * mm});
            skFitSpline(sketch, "E199.MirrorCS", {"points": [v(47.63, -1.14) * mm, v(43.46, -0.92) * mm, v(36.2, -0.67) * mm, v(31.63, -0.53) * mm, v(28, -0.56) * mm], "startDerivative": vector(-16.21, 0.96) * mm, "endDerivative": vector(-16.65, -0.32) * mm});
            skFitSpline(sketch, "E200.MirrorCS", {"points": [v(-47.63, -1.14) * mm, v(-43.46, -0.92) * mm, v(-36.2, -0.67) * mm, v(-31.63, -0.53) * mm, v(-28, -0.56) * mm], "startDerivative": vector(16.21, 0.96) * mm, "endDerivative": vector(16.65, -0.32) * mm});
            skSolve(sketch);
        }
        {
            var Q0;
            Q0 = qSketchRegion(id + "F0", true);
            extrude(context, id + "F1", {"entities" : qUnion([Q0]), "depth" : 50 * mm});
        }
    });
